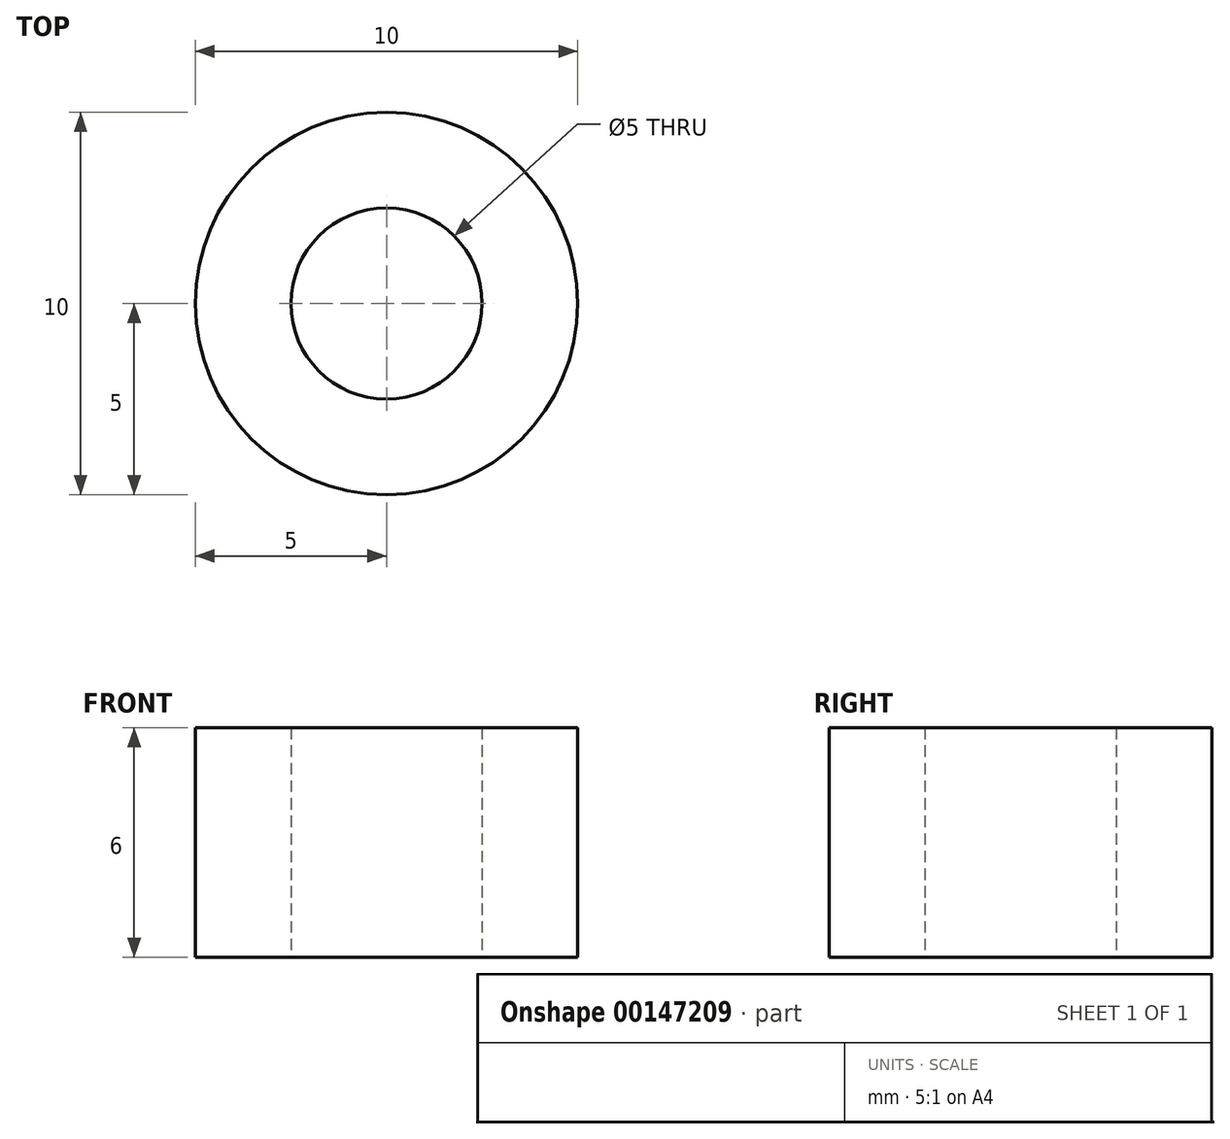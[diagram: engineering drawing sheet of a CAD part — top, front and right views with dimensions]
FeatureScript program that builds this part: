
annotation { "Feature Type Name" : "Feature", "Feature Type Description" : "" }
export const myFeature = defineFeature(function(context is Context, id is Id, definition is map)
    precondition{}
    {
        {
            var Q0;
            Q0=qCreatedBy(makeId("Top.planeOp"),FACE);
            var sketch = newSketch(context, id + "F0", { "sketchPlane" : qUnion([Q0])});
            skCircle(sketch, "E0", {"center": v(0, 0) * mm, "radius": 5 * mm});
            skCircle(sketch, "E1", {"center": v(0, 0) * mm, "radius": 2.5 * mm});
            skSolve(sketch);
        }
        {
            var Q0;
            Q0 = qSketchRegion(id + "F0", true);
            extrude(context, id + "F1", {"entities" : qUnion([Q0]), "depth" : 6 * mm});
        }
    });
